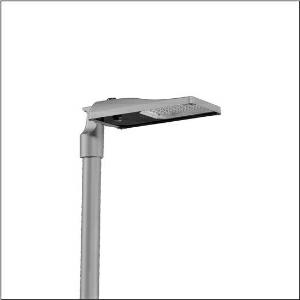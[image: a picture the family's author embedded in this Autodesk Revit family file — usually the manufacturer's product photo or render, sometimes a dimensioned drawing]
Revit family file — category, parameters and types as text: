
# Revit family: streetlight_sl_31_mini___p0_8a_5xh6u31t08ja_d345
name_source: partatom
category: Lighting Fixtures
units: mm (PartAtom-declared; Revit-internal decimal feet)

## family parameters
Cut with Voids When Loaded = No
Host = Face
Light Source = No
Part Type = Normal
Room Calculation Point = No
Round Connector Dimension = Use Diameter
Shared = No

## types (1)
- --- (1 x LED, 12370 lm, 82.5 W, 3000K)
    Apparent Load = 83 VA
    CIE Flux Codes = 36 69 97 100 100
    Color Rendering = 70
    Color Temperature = 3000K
    Default Elevation = 1800 mm
    Description = Streetlight SL 31 mini D4i, Desk-Remote mast luminaire for post-top, side-entry; light control with lens of PMMA; light distribution: P0.8a, direct asymmetric distribution, for standard-compliant lighting for roads and squares; LED: luminous flux: 12.370lm, light colour: 730, colour temperature: 3000K; luminous efficacy: 149,9lm/W; control: pre-setting: logarithmic dimming characteristic, flexible luminous flux parameterisation, time-dependent luminous flux control, constant luminous flux control, power reduction, intelligent temperature release in ECG and LED module, overheat protection; luminaire housing, of diecast aluminium, Siteco® metallic grey (DB 702S), corrosivity category C5 high according to DIN EN ISO 12944; cover of toughened safety glass, transparent, opened without tools; mast flange of diecast aluminium, Siteco® metallic grey (DB 702S), spigot size: 76/60mm, mast flange included unmounted; with cable H07RN-F 2x 1.5mm², cable length: 10,5m, connection cable pre-assembled; mains connection: 220..240V, AC, 50/60Hz; power consumption (at start of service life): 82,5W / (at end of service life): 90,1W / (with reduced operation 50%): 36,8W; protection rating (complete): IP66; insulation class (complete): insulation class II (safety insulation); impact resistance: IK09; certification: CE, ENEC, ENEC+, VDE, UKCA, ZD4i; permissible operating ambient temperature for outdoor applications: -40..+50°C; packaging unit: 1 piece

Light Distribution: P0.8a
    Height = 76 mm
    Lamp = 1 x LED
    Lamp Light Flux = 12370 lm
    Lamp Power = 82.5 W
    Lamp count = 1
    Length = 547 mm
    Luminous efficacy = 150 lm/W
    Manufacturer = Siteco
    ModVariant = No
    Model = 5XH6U31T08JA
    Number of Poles = 1
    OnlyDefault = Yes
    Power Factor = 1
    Product Name = Streetlight SL 31 mini | P0.8a
    Product group = mast luminaire | pylon top
    ProductGroupID = 6100
    Protection Class = Protection class II
    Protection Degree = IP 66
    RLX_Detail_Level = 1
    RLX_Emergency_Light_Flux = 0 lm
    RLX_Emergency_Type = 0
    RLX_Emergency_Type_DB = No
    RlxData = <blob elided: 39825 chars, md5=bdce4ef4>
    Socket = socket
    Standby Power = 0 W
    System Light Flux = 12370 lm
    System Power = 83 W
    Type Comments = factory setting: luminous flux: 100 % | dim-lin: 254 | 870 mA
    Type Image = l_1300332.jpg
    URL = http://relux.com
    VarID = @adj_078797
    Voltage = 0 V
    Weight = 0.00 kg
    Width = 265 mm

## geometry (parser evidence)
native form markers: Blend x4, Sweep x9
no freeform markers — native parametric forms only
